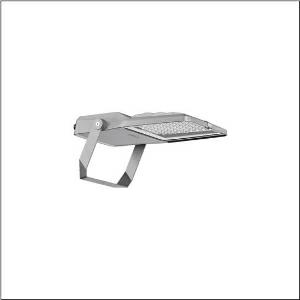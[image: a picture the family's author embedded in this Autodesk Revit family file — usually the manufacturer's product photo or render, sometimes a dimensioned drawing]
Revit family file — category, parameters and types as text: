
# Revit family: floodlight_fl_21_iq_mini___pl52_5xa7771d4d1a_c00e
name_source: partatom
category: Lighting Fixtures
units: mm (PartAtom-declared; Revit-internal decimal feet)

## family parameters
Cut with Voids When Loaded = No
Host = Face
Light Source = No
Part Type = Normal
Room Calculation Point = No
Round Connector Dimension = Use Diameter
Shared = No

## types (1)
- --- (1 x LED, 18610 lm, 143 W, 4000K)
    Apparent Load = 143 VA
    CIE Flux Codes = 26 60 98 100 100
    Color Rendering = 70
    Color Temperature = 4000K
    Default Elevation = 1800 mm
    Description = Floodlight FL 21 iQ mini, floodlight, primary light control with lens, of PMMA, primary optical cover: protective disc, of toughened safety glass, transparent, light distribution: PL52, light emission: direct distribution, installation type: surface-mounted, LED, High Power LED, rated luminous flux: 18.610lm, luminous efficacy: 130lm/W, light colour: 740, colour temperature: 4000K, control gear: iQ Comfort/DALI, control: Auto-Match, Temp-Guard, Lumen-Switch, Night-Set, Smart-Wire, Light-Fading, Desk-Remote (wireless, voltage-free reading and setting of iQ features in the workshop via application-optimized NFC function/RFID function), optimised constant luminous flux control (CLO 2.0), with terminal, 6-pole, mains connection: 220..240V, AC, 50/60Hz, start of lifetime: 143W, end of service life: 152W, reduction: 61W, luminaire housing, of diecast aluminium, powder-coated, Siteco® metallic grey (DB 702S), corrosivity category C5 mid according to DIN EN ISO 12944, suitable for swimming pools, chlorine-resistant, sealing non-destructively replaceable, mounting bracket, of steel, galvanised, powder-coated, Siteco® metallic grey (DB 702S), protection rating (complete): IP66, insulation class (complete): insulation class II (safety insulation), certification: CE, ENEC, VDE, protection symbol: D, impact resistance: IK08, permissible operating ambient temperature: -40..+40°C, permissible operating ambient temperature for outdoor applications: -40..+50°C, standard: DIN EN 12944, LABS conformity tested according to VDMA 24364:2018-05, packaging unit: 1 piece

Light Distribution: PL52
    Height = 70 mm
    Lamp = 1 x LED
    Lamp Light Flux = 18610 lm
    Lamp Power = 143 W
    Lamp count = 1
    Length = 485 mm
    Luminous efficacy = 130 lm/W
    Manufacturer = Siteco
    ModVariant = No
    Model = 5XA7771D4D1A
    Number of Poles = 1
    OnlyDefault = Yes
    Power Factor = 1
    Product Name = Floodlight FL 21 iQ mini | PL52
    Product group = floodlight | pylon annexe
    ProductGroupID = 6200
    Protection Class = Protection class II
    Protection Degree = IP 66
    RLX_Detail_Level = 1
    RLX_Emergency_Light_Flux = 0 lm
    RLX_Emergency_Type = 0
    RLX_Emergency_Type_DB = No
    RlxData = <blob elided: 96825 chars, md5=2ba27915>
    Socket = socket
    Standby Power = 0 W
    System Light Flux = 18610 lm
    System Power = 143 W
    Type Comments = factory setting: luminous flux: 100 % | dim-lin: 254 | 730 mA
    Type Image = l_1006845.jpg
    URL = http://relux.com
    VarID = @adj_163940
    Voltage = 0 V
    Weight = 0.00 kg
    Width = 337 mm

## geometry (parser evidence)
native form markers: Blend x4, Sweep x10
no freeform markers — native parametric forms only
